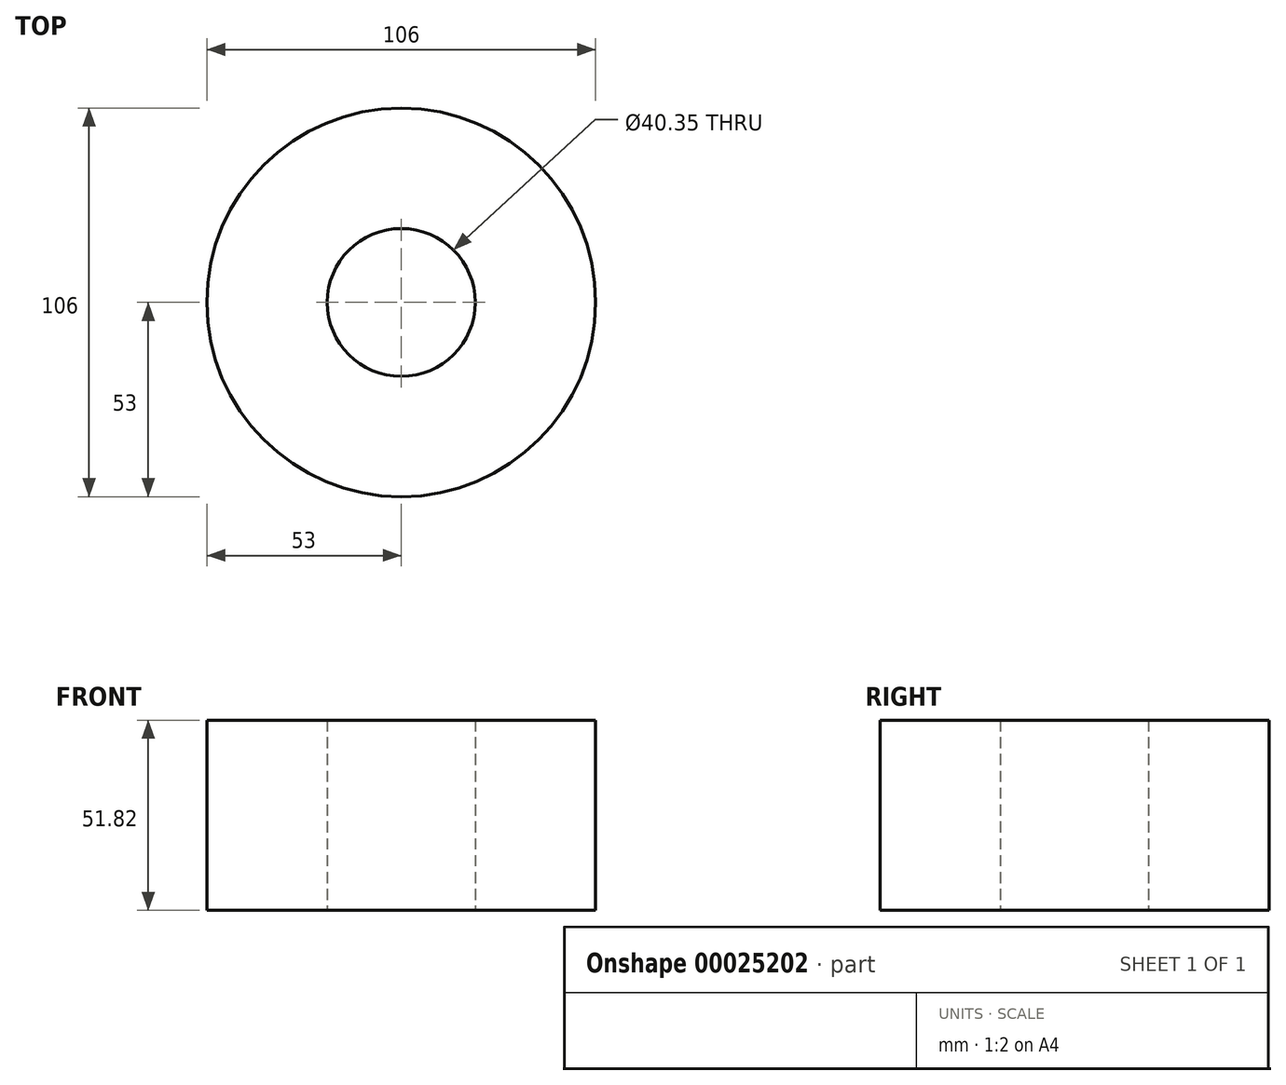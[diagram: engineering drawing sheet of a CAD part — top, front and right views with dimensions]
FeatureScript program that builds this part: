
annotation { "Feature Type Name" : "Feature", "Feature Type Description" : "" }
export const myFeature = defineFeature(function(context is Context, id is Id, definition is map)
    precondition{}
    {
        {
            var Q0;
            Q0=qCreatedBy(makeId("Top.planeOp"),FACE);
            var sketch = newSketch(context, id + "F0", { "sketchPlane" : qUnion([Q0])});
            skCircle(sketch, "E0", {"center": v(0, 0) * mm, "radius": 53 * mm});
            skSolve(sketch);
        }
        {
            var Q0;
            Q0=makeQuery(id+"F0.imprint","IMPRINT",FACE,{"disambiguationData":[TD([[makeQuery(id+"F0.imprint","IMPRINT",EDGE,{"derivedFrom":sQuery(id+"F0.wireOp",EDGE,"E0")}),1.0]])]});
            extrude(context, id + "F1", {"entities" : qUnion([Q0]), "depth" : 51.82 * mm});
        }
        {
            var Q0;
            Q0=makeQuery(id+"F1.opExtrude","CAP_FACE",FACE,{"disambiguationData":[OSD([sQuery(id+"F0.wireOp",EDGE,"E0")])],"isStart":true});
            var sketch = newSketch(context, id + "F2", { "sketchPlane" : qUnion([Q0])});
            skSolve(sketch);
        }
        {
            var Q0;
            Q0=makeQuery(id+"F2.imprint","IMPRINT",FACE,{"disambiguationData":[TD([[makeQuery(id+"F2.imprint","IMPRINT",EDGE,{"derivedFrom":makeQuery(id+"F1.opExtrude","CAP_EDGE",EDGE,{"disambiguationData":[OSD([sQuery(id+"F0.wireOp",EDGE,"E0")])],"isStart":true})}),-1.0]])]});
            var sketch = newSketch(context, id + "F3", { "sketchPlane" : qUnion([Q0])});
            skCircle(sketch, "E1", {"center": v(0, 0) * mm, "radius": 20.17 * mm});
            skSolve(sketch);
        }
        {
            var Q0;
            Q0=makeQuery(id+"F3.imprint","IMPRINT",FACE,{"disambiguationData":[TD([[makeQuery(id+"F3.imprint","IMPRINT",EDGE,{"derivedFrom":sQuery(id+"F3.wireOp",EDGE,"E1")}),1.0]])]});
            extrude(context, id + "F4", {"entities" : qUnion([Q0]), "operationType" : NewBodyOperationType.REMOVE, "oppositeDirection" : true, "depth" : 110.67 * mm});
        }
    });
